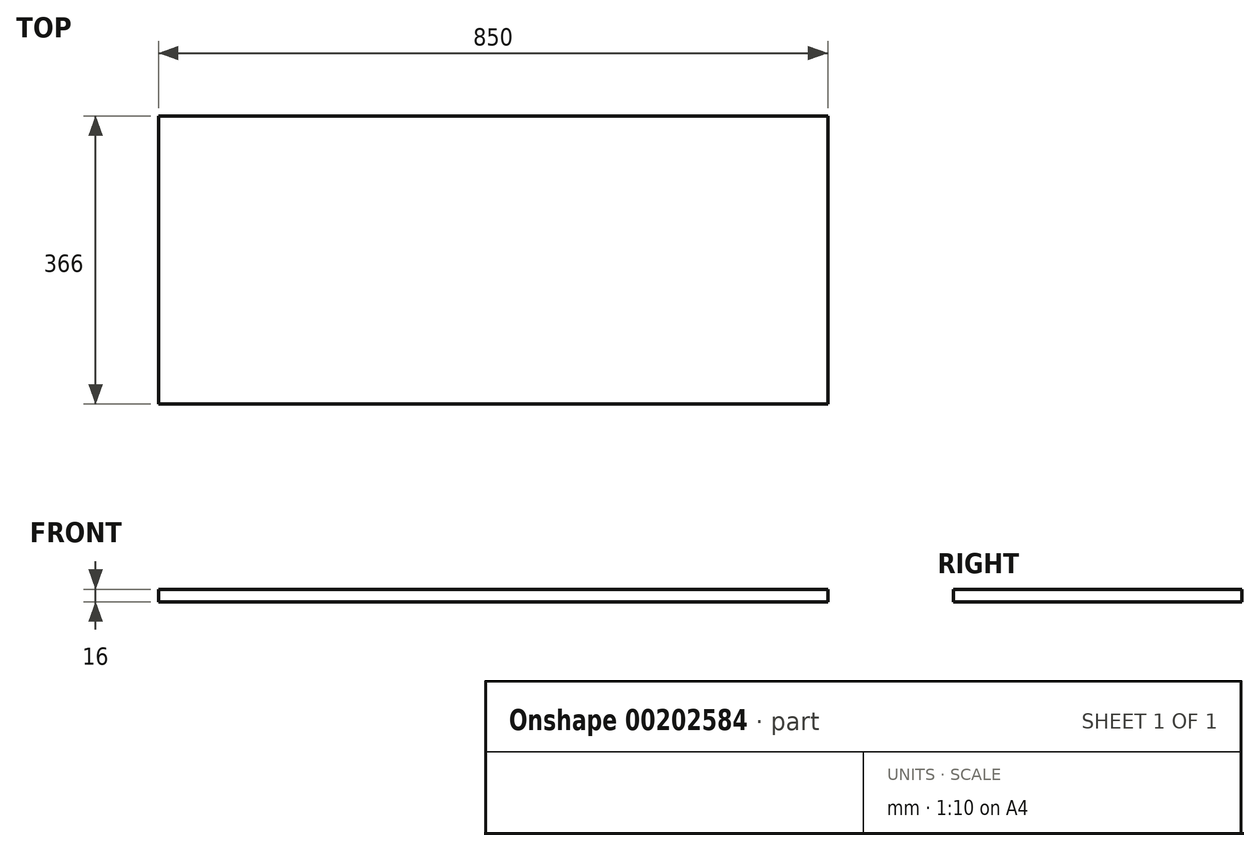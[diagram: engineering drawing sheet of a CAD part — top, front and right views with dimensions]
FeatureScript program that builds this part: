
annotation { "Feature Type Name" : "Feature", "Feature Type Description" : "" }
export const myFeature = defineFeature(function(context is Context, id is Id, definition is map)
    precondition{}
    {
        {
            var Q0;
            Q0=qCreatedBy(makeId("Top.planeOp"),FACE);
            var sketch = newSketch(context, id + "F0", { "sketchPlane" : qUnion([Q0])});
            skLineSegment(sketch, "E0.bottom", {"start": v(-864.34, -235.28) * mm, "end": v(-14.34, -235.28) * mm});
            skLineSegment(sketch, "E0.top", {"start": v(-864.34, 130.72) * mm, "end": v(-14.34, 130.72) * mm});
            skLineSegment(sketch, "E0.left", {"start": v(-864.34, -235.28) * mm, "end": v(-864.34, 130.72) * mm});
            skLineSegment(sketch, "E0.right", {"start": v(-14.34, -235.28) * mm, "end": v(-14.34, 130.72) * mm});
            skSolve(sketch);
        }
        {
            var Q0;
            Q0=makeQuery(id+"F0.imprint","IMPRINT",FACE,{"disambiguationData":[TD([[makeQuery(id+"F0.imprint","IMPRINT",EDGE,{"derivedFrom":sQuery(id+"F0.wireOp",EDGE,"E0.bottom")}),1.0]])]});
            extrude(context, id + "F1", {"entities" : qUnion([Q0]), "depth" : 16 * mm});
        }
    });
